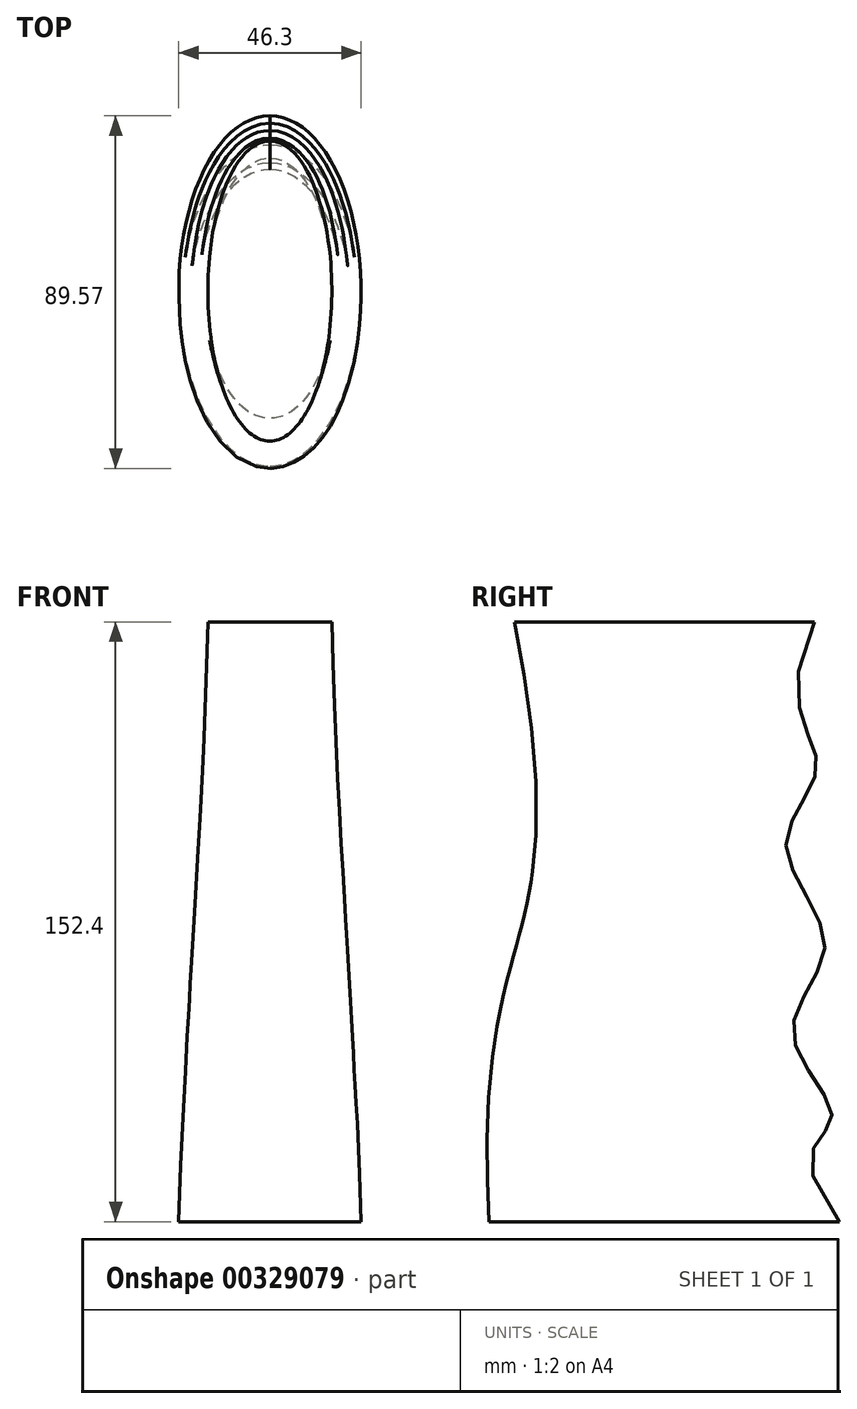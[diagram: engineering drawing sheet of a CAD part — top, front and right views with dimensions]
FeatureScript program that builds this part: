
annotation { "Feature Type Name" : "Feature", "Feature Type Description" : "" }
export const myFeature = defineFeature(function(context is Context, id is Id, definition is map)
    precondition{}
    {
        {
            var Q0;
            Q0=qCreatedBy(makeId("Top.planeOp"),FACE);
            var sketch = newSketch(context, id + "F0", { "sketchPlane" : qUnion([Q0])});
            skEllipse(sketch, "E0", {"center": v(0, 0) * mm, "majorRadius": 44.5 * mm, "minorRadius": 23.15 * mm, "majorAxis": v(0, 1)});
            skPoint(sketch, "E1", {"position": v(0, 44.5) * mm});
            skPoint(sketch, "E2", {"position": v(0, -44.5) * mm});
            skSolve(sketch);
        }
        {
            var Q0;
            Q0=qCreatedBy(makeId("Top.planeOp"),FACE);
            cPlane(context, id + "F1", {"entities" : qUnion([Q0]), "cplaneType" : CPlaneType.OFFSET, "offset" : 152.4 * mm, "width" : 152.4 * mm, "height" : 152.4 * mm});
        }
        {
            var Q0;
            Q0=qCreatedBy(id+"F1.planeOp",FACE);
            var sketch = newSketch(context, id + "F2", { "sketchPlane" : qUnion([Q0])});
            skEllipse(sketch, "E3", {"center": v(0, 0) * mm, "majorRadius": 38.12 * mm, "minorRadius": 15.75 * mm, "majorAxis": v(0, 1)});
            skPoint(sketch, "E4", {"position": v(0, -38.12) * mm});
            skPoint(sketch, "E5", {"position": v(0, 38.12) * mm});
            skSolve(sketch);
        }
        {
            var Q0;
            Q0=qCreatedBy(makeId("Right.planeOp"),FACE);
            var sketch = newSketch(context, id + "F3", { "sketchPlane" : qUnion([Q0])});
            skFitSpline(sketch, "E6", {"points": [v(-38.12, 152.4) * mm, v(-44.5, 0) * mm], "startDerivative": vector(52.7, -264.12) * mm, "endDerivative": vector(14.5, -246.63) * mm});
            skFitSpline(sketch, "E7", {"points": [v(38.12, 152.4) * mm, v(38.8, 115.55) * mm, v(30.95, 95.76) * mm, v(40.78, 70.2) * mm, v(32.66, 47.8) * mm, v(42.58, 26.51) * mm, v(44.5, 0) * mm], "startDerivative": vector(-158.78, -336.73) * mm, "endDerivative": vector(267.25, -339.53) * mm});
            skSolve(sketch);
        }
        {
            var Q0;
            Q0=makeQuery(id+"F2.imprint","IMPRINT",FACE,{"disambiguationData":[TD([[makeQuery(id+"F2.imprint","IMPRINT",EDGE,{"derivedFrom":sQuery(id+"F2.wireOp",EDGE,"E3")}),1.0]])]});
            var Q1;
            Q1=makeQuery(id+"F0.imprint","IMPRINT",FACE,{"disambiguationData":[TD([[makeQuery(id+"F0.imprint","IMPRINT",EDGE,{"derivedFrom":sQuery(id+"F0.wireOp",EDGE,"E0")}),1.0]])]});
            var Q2;
            Q2=sQuery(id+"F3.wireOp",EDGE,"E7");
            var Q3;
            Q3=sQuery(id+"F3.wireOp",EDGE,"E6");
            loft(context, id + "F4", {"sheetProfilesArray" : [{ "sheetProfileEntities" : qUnion([Q0]) }, { "sheetProfileEntities" : qUnion([Q1]) }], "addGuides" : true, "guidesArray" : [{ "guideEntities" : qUnion([Q2]), "guideDerivativeType" : LoftGuideDerivativeType.DEFAULT, "guideDerivativeMagnitude" : 1 }, { "guideEntities" : qUnion([Q3]), "guideDerivativeType" : LoftGuideDerivativeType.DEFAULT, "guideDerivativeMagnitude" : 1 }]});
        }
    });
